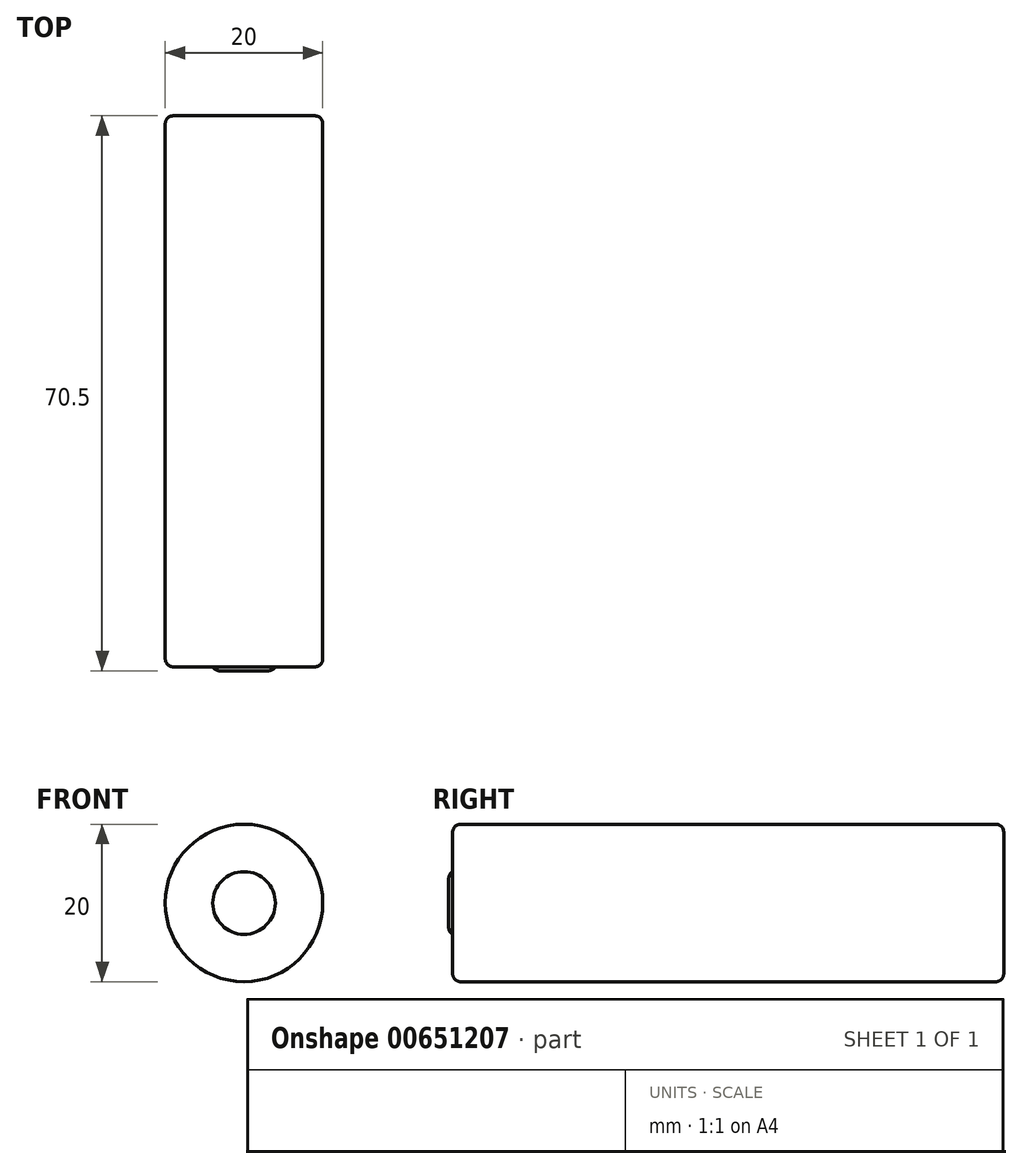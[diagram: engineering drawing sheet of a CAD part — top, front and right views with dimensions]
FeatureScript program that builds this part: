
annotation { "Feature Type Name" : "Feature", "Feature Type Description" : "" }
export const myFeature = defineFeature(function(context is Context, id is Id, definition is map)
    precondition{}
    {
        {
            var Q0;
            Q0=qCreatedBy(makeId("Front.planeOp"),FACE);
            var sketch = newSketch(context, id + "F0", { "sketchPlane" : qUnion([Q0])});
            skCircle(sketch, "E0", {"center": v(0, 0) * mm, "radius": 10 * mm});
            skSolve(sketch);
        }
        {
            var Q0;
            Q0=makeQuery(id+"F0.imprint","IMPRINT",FACE,{"disambiguationData":[TD([[makeQuery(id+"F0.imprint","IMPRINT",EDGE,{"derivedFrom":sQuery(id+"F0.wireOp",EDGE,"E0")}),1.0]])]});
            extrude(context, id + "F1", {"entities" : qUnion([Q0]), "depth" : 70 * mm, "offsetDistance" : 25 * mm});
        }
        {
            var Q0;
            Q0=makeQuery(id+"F1.opExtrude","CAP_EDGE",EDGE,{"disambiguationData":[OSD([sQuery(id+"F0.wireOp",EDGE,"E0")])],"isStart":false});
            var Q1;
            Q1=makeQuery(id+"F1.opExtrude","CAP_EDGE",EDGE,{"disambiguationData":[OSD([sQuery(id+"F0.wireOp",EDGE,"E0")])],"isStart":true});
            fillet(context, id + "F2", {"entities" : qUnion([Q0, Q1]), "tangentPropagation" : true, "radius" : 1 * mm, "defaultsChanged" : true, "vertexSettings" : [], "allowEdgeOverflow" : false});
        }
        {
            var Q0;
            Q0=makeQuery(id+"F1.opExtrude","CAP_FACE",FACE,{"disambiguationData":[OSD([sQuery(id+"F0.wireOp",EDGE,"E0")])],"isStart":false});
            var sketch = newSketch(context, id + "F3", { "sketchPlane" : qUnion([Q0])});
            skCircle(sketch, "E1", {"center": v(0, 0) * mm, "radius": 3.98 * mm});
            skSolve(sketch);
        }
        {
            var Q0;
            Q0=makeQuery(id+"F3.imprint","IMPRINT",FACE,{"disambiguationData":[TD([[makeQuery(id+"F3.imprint","IMPRINT",EDGE,{"derivedFrom":sQuery(id+"F3.wireOp",EDGE,"E1")}),1.0]])]});
            extrude(context, id + "F4", {"entities" : qUnion([Q0]), "operationType" : NewBodyOperationType.ADD, "depth" : 0.5 * mm, "offsetDistance" : 25 * mm});
        }
        {
            var Q0;
            Q0=makeQuery(id+"F4.opExtrude","CAP_FACE",FACE,{"disambiguationData":[OSD([sQuery(id+"F3.wireOp",EDGE,"E1")])],"isStart":false});
            fillet(context, id + "F5", {"entities" : qUnion([Q0]), "tangentPropagation" : true, "radius" : 1 * mm, "defaultsChanged" : true, "vertexSettings" : [], "allowEdgeOverflow" : false});
        }
    });
